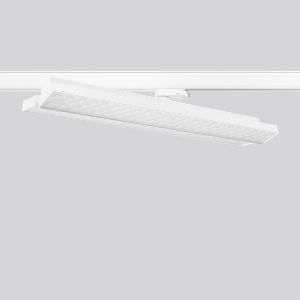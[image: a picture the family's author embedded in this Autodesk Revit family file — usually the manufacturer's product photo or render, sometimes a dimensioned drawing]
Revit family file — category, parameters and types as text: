
# Revit family: tx-move_742161_002_f608
name_source: partatom
category: Lighting Fixtures
units: mm (PartAtom-declared; Revit-internal decimal feet)

## family parameters
Cut with Voids When Loaded = No
Host = Face
Light Source = No
Part Type = Normal
Room Calculation Point = No
Round Connector Dimension = Use Diameter
Shared = No

## types (1)
- MultiLumen 1 (1 x LED Modul 830, 2900 lm, 3000)
    Apparent Load = 41 VA
    CIE Flux Codes = 90 97 99 100 100
    Color Rendering = 80
    Color Temperature = 3000
    Default Elevation = 1800 mm
    Description = Series: TX-MOVE
Multifunctional surface-mounted spotlight for area lighting. Very flat design. Housing: sheet steel, powder-coated. Rotation range: 356°. Swivel range: 90°. Consistent alignment possible with visible tilt scale. High-efficiency LED units with optimum light control thanks to clear plastic (PC) lens optics. Spezielle Mikrostrukturen reduzieren Gelbsaum. Symmetrical light distribution. With multi adaptor for 3-circuit tracks 230 V. Suitable for Track on ceiling. MultiLumen: Luminous flux adjustable in 3 steps. Factory setting is the highest luminous flux. Environmentally friendly and resource-saving due to replaceable and recyclable components. Very good glare control, ideal for till areas. 
Colour: traffic white, matt (RAL 9016)
Length: 570 mm
Width: 119 mm
Height: 92 mm
Lamp: LED
Socket: without socket
Colour temperature: 3000K
Colour rendering index (CRI): 80
System power: 41 W
Rated luminous flux: 5800 lm
Luminous efficiency: 141 lm/W
System power 2: 57 W
Rated luminous flux 2: 7850 lm
Luminous efficiency 2: 138 lm/W
System power 3: 73 W
Rated luminous flux 3: 9600 lm
Luminous efficiency 3: 132 lm/W
Control gear: Regulated power supply
Protection class: I
Type of protection: IP 20
    Height = 75 mm
    Lamp = 1 x LED Modul 830
    Lamp Light Flux = 2900 lm
    Lamp count = 1
    Length = 569 mm
    Lifetime = 50000 h
    Luminous efficacy = 141 lm/W
    Manufacturer = RZB
    ModVariant = No
    Model = 742161.002
    Mounting Place = Ceiling
    Mounting Type = Surface mounted
    Number of Poles = 1
    OnlyDefault = Yes
    Power Factor = 1
    Product Name = TX-MOVE
    Product group = Track mounted projectors
    ProductGroupID = 301
    Protection Class = Protection class I
    Protection Degree = IP 20
    RLX_Detail_Level = 1
    RLX_Emergency_Light_Flux = 0 lm
    RLX_Emergency_Type = 0
    RLX_Emergency_Type_DB = No
    RlxData = <blob elided: 31245 chars, md5=155a0752>
    Socket = socket
    Standby Power = 0 W
    System Light Flux = 5800 lm
    System Power = 41 W
    Type Comments = MultiLumen 1
    Type Image = 742162.002.jpg
    URL = http://relux.com
    VarID = multilumen_1
    Voltage = 0 V
    Weight = 0.00 kg
    Width = 119 mm

## geometry (parser evidence)
native form markers: Blend x4, Sweep x15
no freeform markers — native parametric forms only
